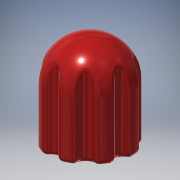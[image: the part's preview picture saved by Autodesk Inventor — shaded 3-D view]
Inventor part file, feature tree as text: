
AUTODESK INVENTOR PART (.ipt)
format: ipt  version: 2018 (Build 220112000, 112)  size: 413,184 bytes
history: native  units: mm
features: sketch x2, revolve x1, extrude x1, fillet x1
ambient origin geometry x8: Origin, YZ Plane, XZ Plane, XY Plane, X Axis, Y Axis, Z Axis, Center Point
bodies: Solid1 (feature_tree)
feature tree (5):
  revolve  "Revolution1"  [1 undecoded]
  extrude  "Extrusion1"  Depth=2.0mm
  fillet  "Fillet1"  Radius=2.0mm
  sketch  "Sketch1"  dims[d0=5.0mm d1=17.0mm]
  sketch  "Sketch2"  dims[d2=21.13mm d3=23.0mm d4=2.0mm d5=1.0mm d6=90.0deg d7=17.0mm d8=6.0mm d9=80.0mm d11=360.0deg d13=10.0mm d14=0.0mm d15=2.0mm]
note: 1 required parameter value undecoded (feature->parameter linkage not recoverable at this tier; creation-order binding heuristic only, values carry confidence <= 0.55)
